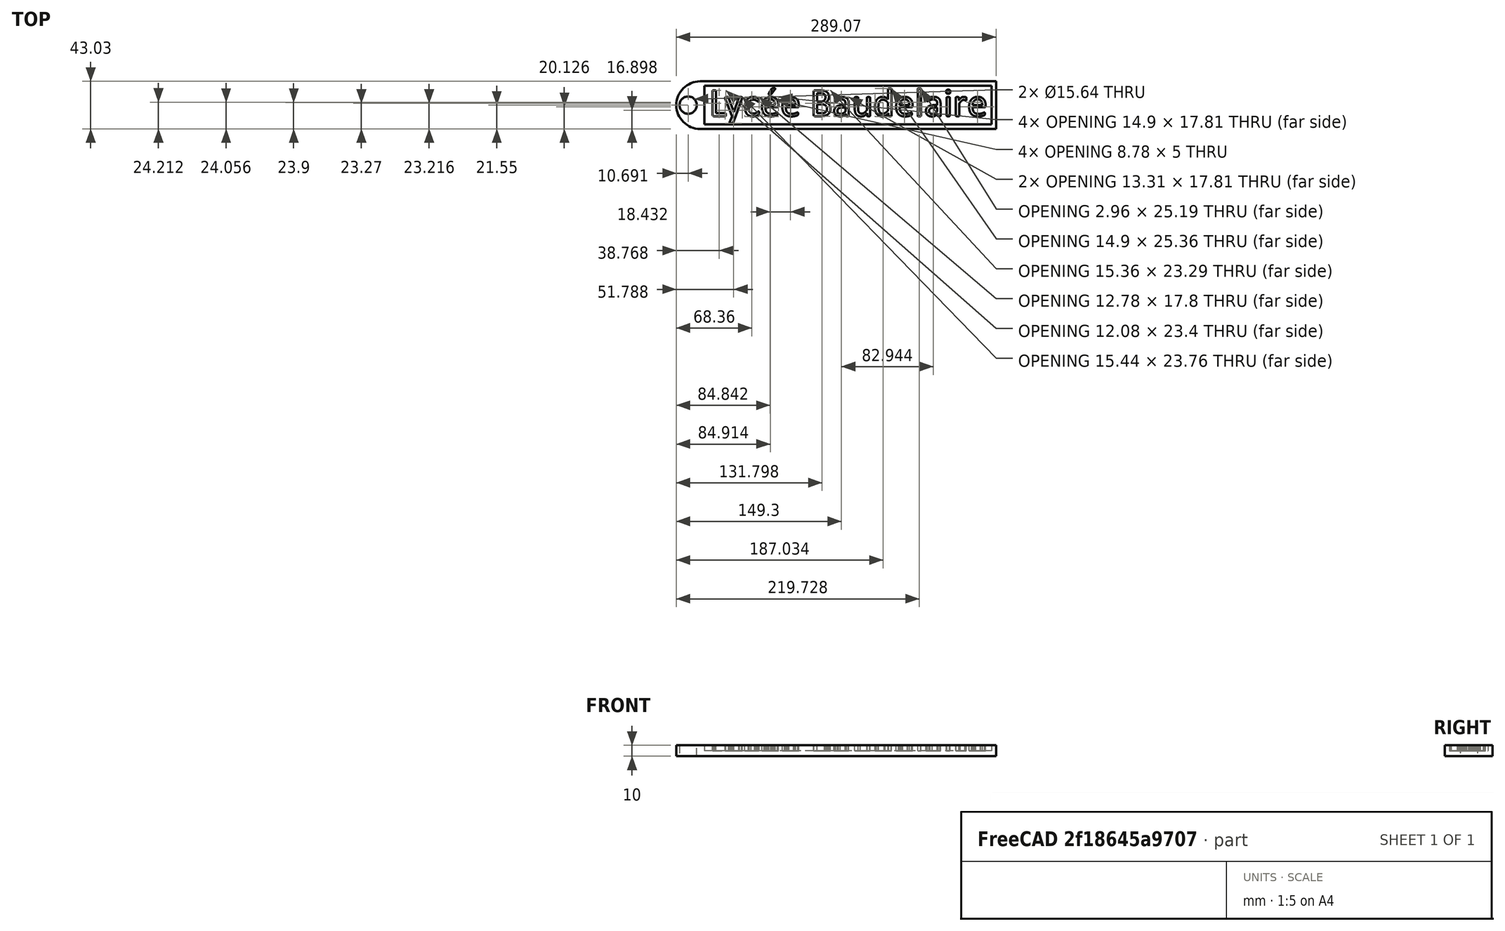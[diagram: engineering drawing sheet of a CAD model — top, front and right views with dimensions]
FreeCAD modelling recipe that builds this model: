
FCSTD DOCUMENT  (FreeCAD 0.16R6712 (Git))
Label: Lycée Baudelaire
License: All rights reserved
LicenseURL: http://en.wikipedia.org/wiki/All_rights_reserved
objects: PartDesign::Pad×2, Sketcher::SketchObject×2, Part::Part2DObjectPython×1, PartDesign::Pocket×1, Part::MultiFuse×1, Mesh::Feature×1
note: 10 computed .brp shape members not serialized (recipe doc carries the construction recipe); baked Part::Feature solids carry a one-line shape summary decoded from their .brp

FEATURE [Part::Part2DObjectPython] ShapeString  # Draft 2D object (typed FeaturePython)
  FontFile = D:/Program Files/FreeCAD/Fonts/calibri.ttf
  Size = 30
  String = Lycée Baudelaire
  Tracking = 0
FEATURE [PartDesign::Pad] Pad
  Length = 10
  Length2 = 100
  Sketch = -> ShapeString
  Type = 0
FEATURE [Sketcher::SketchObject] Sketch
  sketch-geometry (11):
    g0: LineSegment StartX=-8.12089 StartY=31.4561 StartZ=0 EndX=259.442 EndY=31.4561 EndZ=0
    g1: LineSegment StartX=259.442 StartY=31.4561 StartZ=0 EndX=259.442 EndY=-11.5696 EndZ=0
    g2: LineSegment StartX=259.442 StartY=-11.5696 StartZ=0 EndX=-8.12089 EndY=-11.5696 EndZ=0
    g3: LineSegment [constr] StartX=-8.12089 StartY=-11.5696 StartZ=0 EndX=-8.12089 EndY=31.4561 EndZ=0
    g4: ArcOfCircle CenterX=-8.12089 CenterY=9.94325 CenterZ=0 NormalX=0 NormalY=0 NormalZ=1 Radius=21.5129 StartAngle=1.5708 EndAngle=4.71239
    g5: Circle CenterX=-18.9385 CenterY=9.97972 CenterZ=0 NormalX=0 NormalY=0 NormalZ=1 Radius=7.8177
    g6: GeomPoint [constr] X=-26.5694 Y=8.28102 Z=0
    g7: GeomPoint [constr] X=-29.5694 Y=8.28102 Z=0
    g8: GeomPoint [constr] X=-11.1209 Y=9.94325 Z=0
    g9: LineSegment [constr] StartX=-29.5694 StartY=8.28102 StartZ=0 EndX=-26.5694 EndY=8.28102 EndZ=0
    g10: LineSegment [constr] StartX=-11.1209 StartY=9.94325 StartZ=0 EndX=-8.12089 EndY=9.94325 EndZ=0
  constraints (25):
    c: Coincident(g0,g1)
    c: Coincident(g1,g2)
    c: Coincident(g2,g3)
    c: Coincident(g3,g0)
    c: Horizontal(g0)
    c: Horizontal(g2)
    c: Vertical(g1)
    c: Vertical(g3)
    c: PointOnObject(g4,g3)
    c: Coincident(g4,g0)
    c: DistanceY(g1,g0) = 43.0257
    c: DistanceX(g2,g-1) = 8.12089
    c: DistanceY(g2,g-1) = 11.5696
    c: Coincident(g4,g2)
    c: PointOnObject(g6,g5)
    c: PointOnObject(g8,g5)
    c: DistanceX(g7,g6) = 3
    c: Coincident(g9,g7)
    c: Coincident(g9,g6)
    c: Horizontal(g9)
    c: PointOnObject(g7,g4)
    c: Coincident(g10,g8)
    c: Coincident(g10,g4)
    c: Horizontal(g10)
    c: Equal(g9,g10)
FEATURE [PartDesign::Pad] Pad001
  Length = 10
  Length2 = 100
  Sketch = -> Sketch
  Type = 0
FEATURE [Sketcher::SketchObject] Sketch001
  ExternalGeometry = -> [Pad001]
  Placement = pos=(0,0,10) rot=(0,0,1;0rad)
  Support = -> Pad001 [Face7]
  sketch-geometry (4):
    g0: LineSegment StartX=-4.12089 StartY=27.4561 StartZ=0 EndX=255.442 EndY=27.4561 EndZ=0
    g1: LineSegment StartX=255.442 StartY=27.4561 StartZ=0 EndX=255.442 EndY=-7.5696 EndZ=0
    g2: LineSegment StartX=255.442 StartY=-7.5696 StartZ=0 EndX=-4.12089 EndY=-7.5696 EndZ=0
    g3: LineSegment StartX=-4.12089 StartY=-7.5696 StartZ=0 EndX=-4.12089 EndY=27.4561 EndZ=0
  constraints (12):
    c: Coincident(g0,g1)
    c: Coincident(g1,g2)
    c: Coincident(g2,g3)
    c: Coincident(g3,g0)
    c: Horizontal(g0)
    c: Horizontal(g2)
    c: Vertical(g1)
    c: Vertical(g3)
    c: DistanceX(g1,g-3) = 4
    c: DistanceY(g-3,g1) = 4
    c: DistanceX(g-4,g0) = 4
    c: DistanceY(g0,g-4) = 4
FEATURE [PartDesign::Pocket] Pocket
  Length = 5
  Sketch = -> Sketch001
  Type = 0
FEATURE [Part::MultiFuse] Fusion
  Shapes = -> [Pocket,Pad]
FEATURE [Mesh::Feature] Mesh  label="Fusion (Meshed)"
